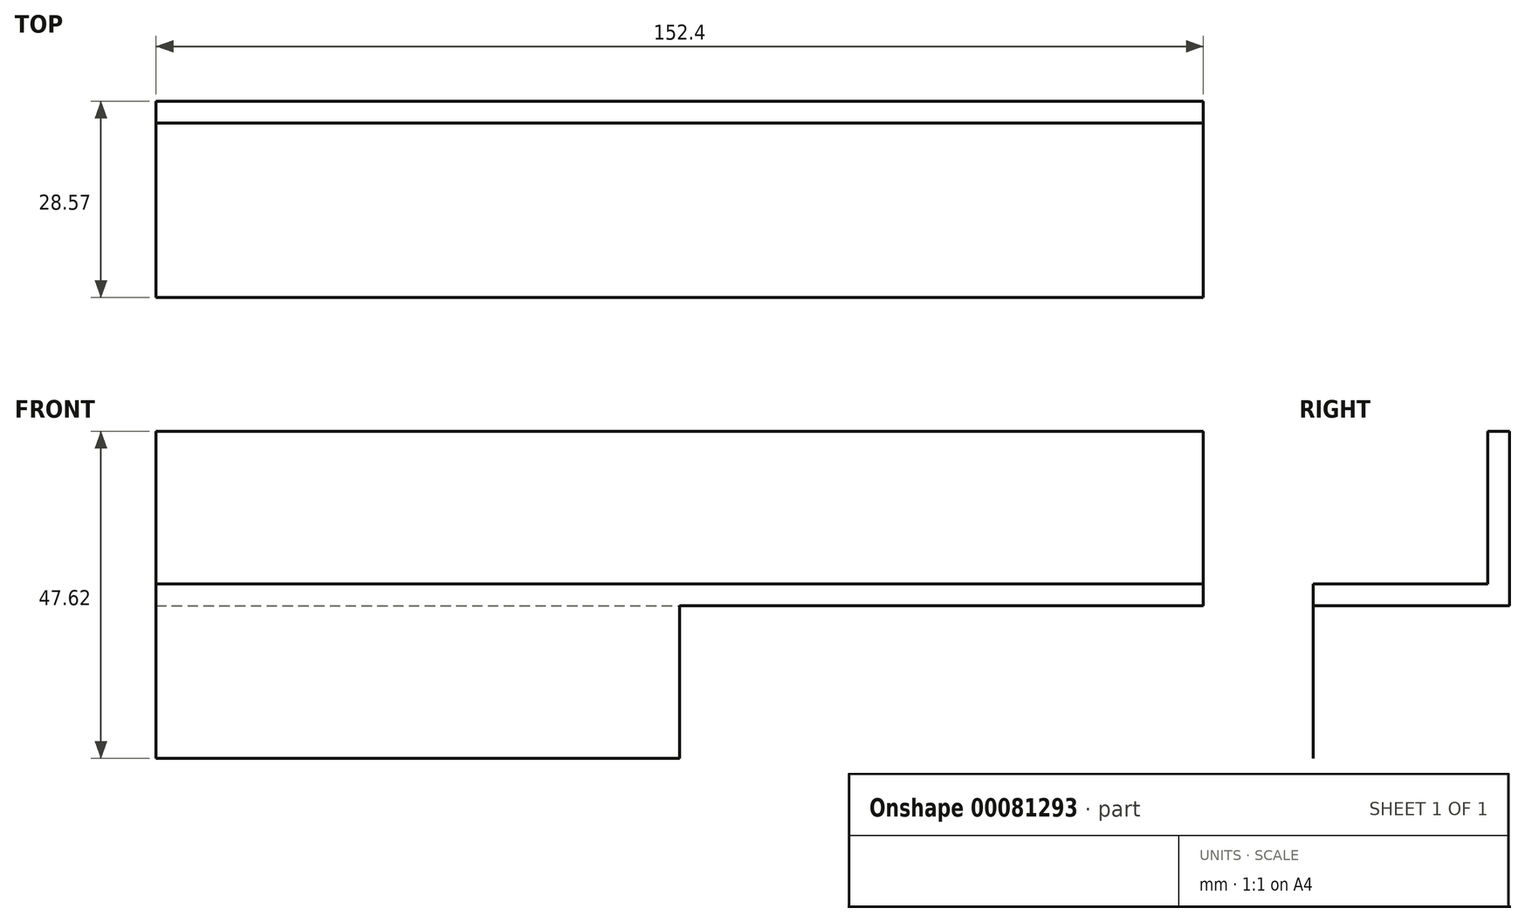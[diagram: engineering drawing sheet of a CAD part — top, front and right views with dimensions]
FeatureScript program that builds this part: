
annotation { "Feature Type Name" : "Feature", "Feature Type Description" : "" }
export const myFeature = defineFeature(function(context is Context, id is Id, definition is map)
    precondition{}
    {
        {
            var Q0;
            Q0=qCreatedBy(makeId("Front.planeOp"),FACE);
            var sketch = newSketch(context, id + "F0", { "sketchPlane" : qUnion([Q0])});
            skLineSegment(sketch, "E0.bottom", {"start": v(-28.07, 54.21) * mm, "end": v(124.33, 54.21) * mm});
            skLineSegment(sketch, "E0.top", {"start": v(-28.07, 28.81) * mm, "end": v(124.33, 28.81) * mm});
            skLineSegment(sketch, "E0.left", {"start": v(-28.07, 54.21) * mm, "end": v(-28.07, 28.81) * mm});
            skLineSegment(sketch, "E0.right", {"start": v(124.33, 54.21) * mm, "end": v(124.33, 28.81) * mm});
            skSolve(sketch);
        }
        {
            var Q0;
            Q0=makeQuery(id+"F0.imprint","IMPRINT",FACE,{"disambiguationData":[TD([[makeQuery(id+"F0.imprint","IMPRINT",EDGE,{"derivedFrom":sQuery(id+"F0.wireOp",EDGE,"E0.bottom")}),-1.0]])]});
            extrude(context, id + "F1", {"entities" : qUnion([Q0]), "depth" : 3.17 * mm});
        }
        {
            var Q0;
            Q0=makeQuery(id+"F1.opExtrude","SWEPT_FACE",FACE,{"disambiguationData":[OSD([sQuery(id+"F0.wireOp",EDGE,"E0.right")])]});
            var sketch = newSketch(context, id + "F2", { "sketchPlane" : qUnion([Q0])});
            skLineSegment(sketch, "E1.bottom", {"start": v(0, 28.81) * mm, "end": v(-28.58, 28.81) * mm});
            skLineSegment(sketch, "E1.top", {"start": v(0, 31.99) * mm, "end": v(-28.58, 31.99) * mm});
            skLineSegment(sketch, "E1.left", {"start": v(0, 28.81) * mm, "end": v(0, 31.99) * mm});
            skLineSegment(sketch, "E1.right", {"start": v(-28.58, 28.81) * mm, "end": v(-28.58, 31.99) * mm});
            skSolve(sketch);
        }
        {
            var Q0;
            {var subQ3=sQuery(id+"F2.wireOp",EDGE,"E1.right");Q0=makeQuery(id+"F2.imprint","IMPRINT",FACE,{"disambiguationData":[TD([[makeQuery(id+"F2.imprint","IMPRINT",EDGE,{"derivedFrom":subQ3}),-1.0]])]});}
            extrude(context, id + "F3", {"entities" : qUnion([Q0]), "operationType" : NewBodyOperationType.ADD, "oppositeDirection" : true, "depth" : 152.4 * mm});
        }
        {
            var Q0;
            Q0=makeQuery(id+"F3.opExtrude","SWEPT_FACE",FACE,{"disambiguationData":[OSD([sQuery(id+"F2.wireOp",EDGE,"E1.right")])]});
            var sketch = newSketch(context, id + "F4", { "sketchPlane" : qUnion([Q0])});
            skLineSegment(sketch, "E2.bottom", {"start": v(-28.07, 31.99) * mm, "end": v(48.13, 31.99) * mm});
            skLineSegment(sketch, "E2.top", {"start": v(-28.07, 6.59) * mm, "end": v(48.13, 6.59) * mm});
            skLineSegment(sketch, "E2.left", {"start": v(-28.07, 31.99) * mm, "end": v(-28.07, 6.59) * mm});
            skLineSegment(sketch, "E2.right", {"start": v(48.13, 31.99) * mm, "end": v(48.13, 6.59) * mm});
            skSolve(sketch);
        }
        {
            var Q0;
            {var subQ0=sQuery(id+"F4.wireOp",EDGE,"E2.top");Q0=makeQuery(id+"F4.imprint","IMPRINT",FACE,{"disambiguationData":[TD([[makeQuery(id+"F4.imprint","IMPRINT",EDGE,{"derivedFrom":subQ0}),1.0]])]});}
            extrude(context, id + "F5", {"entities" : qUnion([Q0]), "operationType" : NewBodyOperationType.ADD, "oppositeDirection" : true, "depth" : 1 / 203.2 * mm});
        }
    });
